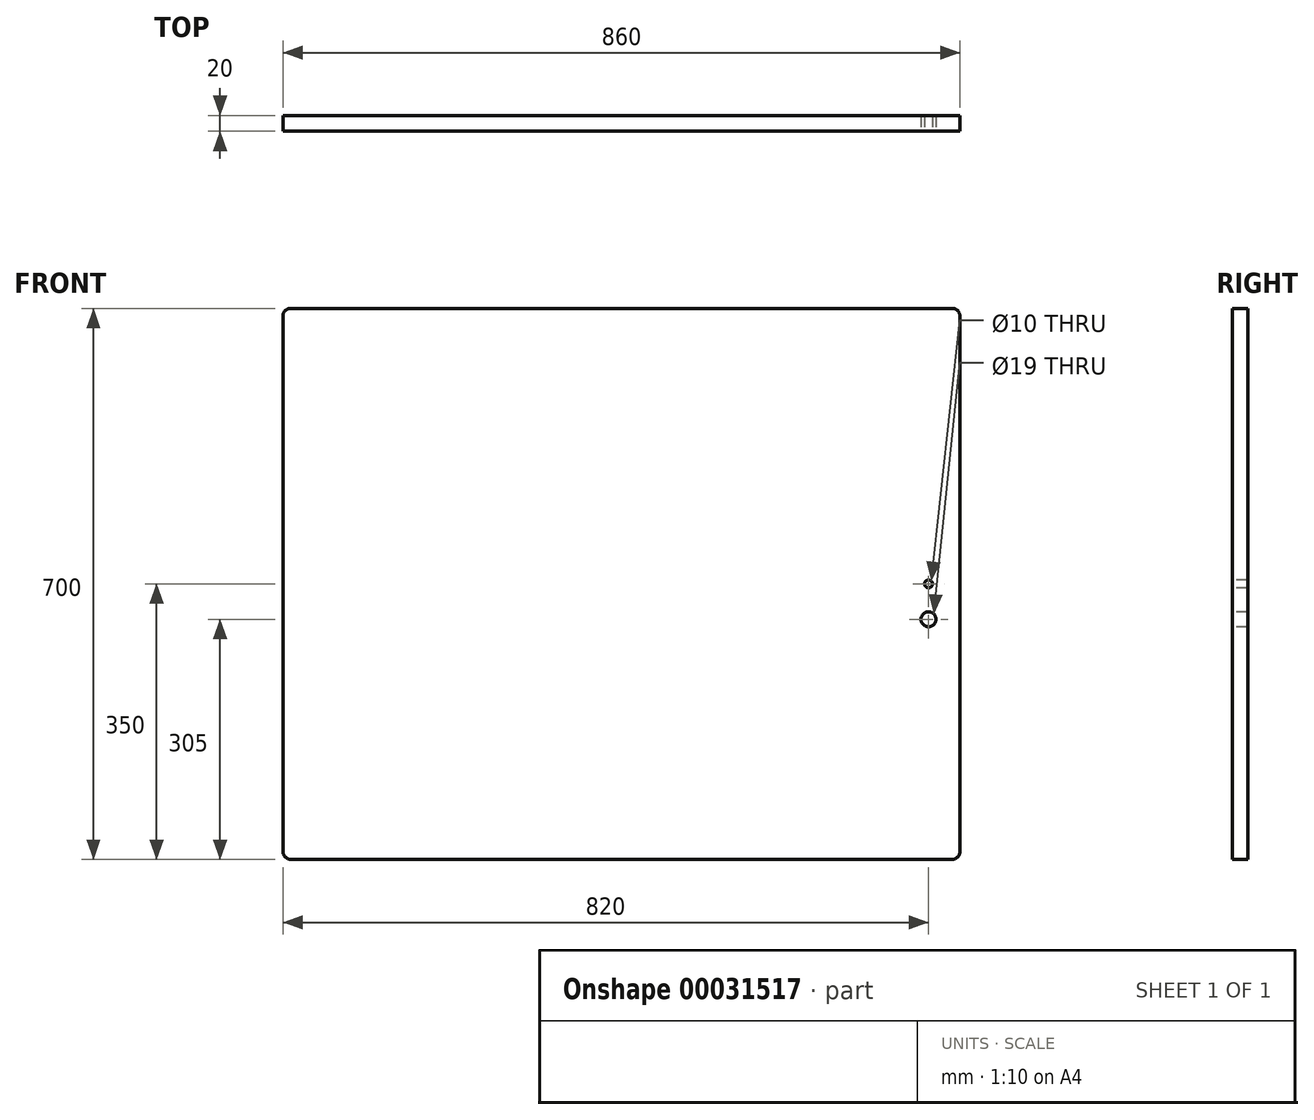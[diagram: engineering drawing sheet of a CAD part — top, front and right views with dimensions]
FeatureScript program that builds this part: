
annotation { "Feature Type Name" : "Feature", "Feature Type Description" : "" }
export const myFeature = defineFeature(function(context is Context, id is Id, definition is map)
    precondition{}
    {
        {
            var Q0;
            Q0=qCreatedBy(makeId("Front.planeOp"),FACE);
            var sketch = newSketch(context, id + "F0", { "sketchPlane" : qUnion([Q0])});
            skLineSegment(sketch, "E0.rect.bottom", {"start": v(430, 350) * mm, "end": v(-430, 350) * mm});
            skLineSegment(sketch, "E0.rect.top", {"start": v(430, -350) * mm, "end": v(-430, -350) * mm});
            skLineSegment(sketch, "E0.rect.left", {"start": v(430, 350) * mm, "end": v(430, -350) * mm});
            skLineSegment(sketch, "E0.rect.right", {"start": v(-430, 350) * mm, "end": v(-430, -350) * mm});
            skPoint(sketch, "E0.rect.middle", {"position": v(0, 0) * mm});
            skSolve(sketch);
        }
        {
            var Q0;
            Q0 = qSketchRegion(id + "F0", true);
            extrude(context, id + "F1", {"entities" : qUnion([Q0]), "depth" : 20 * mm});
        }
        {
            var Q0;
            Q0=makeQuery(id+"F1.opExtrude","CAP_FACE",FACE,{"disambiguationData":[OSD([sQuery(id+"F0.wireOp",EDGE,"E0.rect.bottom"),sQuery(id+"F0.wireOp",EDGE,"E0.rect.top"),sQuery(id+"F0.wireOp",EDGE,"E0.rect.left"),sQuery(id+"F0.wireOp",EDGE,"E0.rect.right")])],"isStart":false});
            var sketch = newSketch(context, id + "F2", { "sketchPlane" : qUnion([Q0])});
            skCircle(sketch, "E1", {"center": v(390, 0) * mm, "radius": 5 * mm});
            skSolve(sketch);
        }
        {
            var Q0;
            Q0=makeQuery(id+"F2.imprint","IMPRINT",FACE,{"disambiguationData":[TD([[makeQuery(id+"F2.imprint","IMPRINT",EDGE,{"derivedFrom":sQuery(id+"F2.wireOp",EDGE,"E1")}),1.0]])]});
            extrude(context, id + "F3", {"entities" : qUnion([Q0]), "operationType" : NewBodyOperationType.REMOVE, "endBound" : BoundingType.THROUGH_ALL, "oppositeDirection" : true, "depth" : 25 * mm});
        }
        {
            var Q0;
            Q0=makeQuery(id+"F1.opExtrude","CAP_FACE",FACE,{"disambiguationData":[OSD([sQuery(id+"F0.wireOp",EDGE,"E0.rect.bottom"),sQuery(id+"F0.wireOp",EDGE,"E0.rect.top"),sQuery(id+"F0.wireOp",EDGE,"E0.rect.left"),sQuery(id+"F0.wireOp",EDGE,"E0.rect.right")])],"isStart":false});
            var sketch = newSketch(context, id + "F4", { "sketchPlane" : qUnion([Q0])});
            skCircle(sketch, "E2", {"center": v(390, -45) * mm, "radius": 9.5 * mm});
            skSolve(sketch);
        }
        {
            var Q0;
            Q0=makeQuery(id+"F4.imprint","IMPRINT",FACE,{"disambiguationData":[TD([[makeQuery(id+"F4.imprint","IMPRINT",EDGE,{"derivedFrom":sQuery(id+"F4.wireOp",EDGE,"E2")}),1.0]])]});
            extrude(context, id + "F5", {"entities" : qUnion([Q0]), "operationType" : NewBodyOperationType.REMOVE, "endBound" : BoundingType.THROUGH_ALL, "oppositeDirection" : true, "depth" : 25 * mm});
        }
        {
            var Q0;
            Q0=makeQuery(id+"F1.opExtrude","SWEPT_EDGE",EDGE,{"disambiguationData":[OSD([sQuery(id+"F0.wireOp",EDGE,"E0.rect.bottom"),sQuery(id+"F0.wireOp",EDGE,"E0.rect.left")])]});
            var Q1;
            Q1=makeQuery(id+"F1.opExtrude","SWEPT_EDGE",EDGE,{"disambiguationData":[OSD([sQuery(id+"F0.wireOp",EDGE,"E0.rect.top"),sQuery(id+"F0.wireOp",EDGE,"E0.rect.left")])]});
            var Q2;
            Q2=makeQuery(id+"F1.opExtrude","SWEPT_EDGE",EDGE,{"disambiguationData":[OSD([sQuery(id+"F0.wireOp",EDGE,"E0.rect.bottom"),sQuery(id+"F0.wireOp",EDGE,"E0.rect.right")])]});
            var Q3;
            Q3=makeQuery(id+"F1.opExtrude","SWEPT_EDGE",EDGE,{"disambiguationData":[OSD([sQuery(id+"F0.wireOp",EDGE,"E0.rect.top"),sQuery(id+"F0.wireOp",EDGE,"E0.rect.right")])]});
            fillet(context, id + "F6", {"entities" : qUnion([Q0, Q1, Q2, Q3]), "radius" : 10 * mm, "tangentPropagation" : true, "allowEdgeOverflow" : false});
        }
    });
